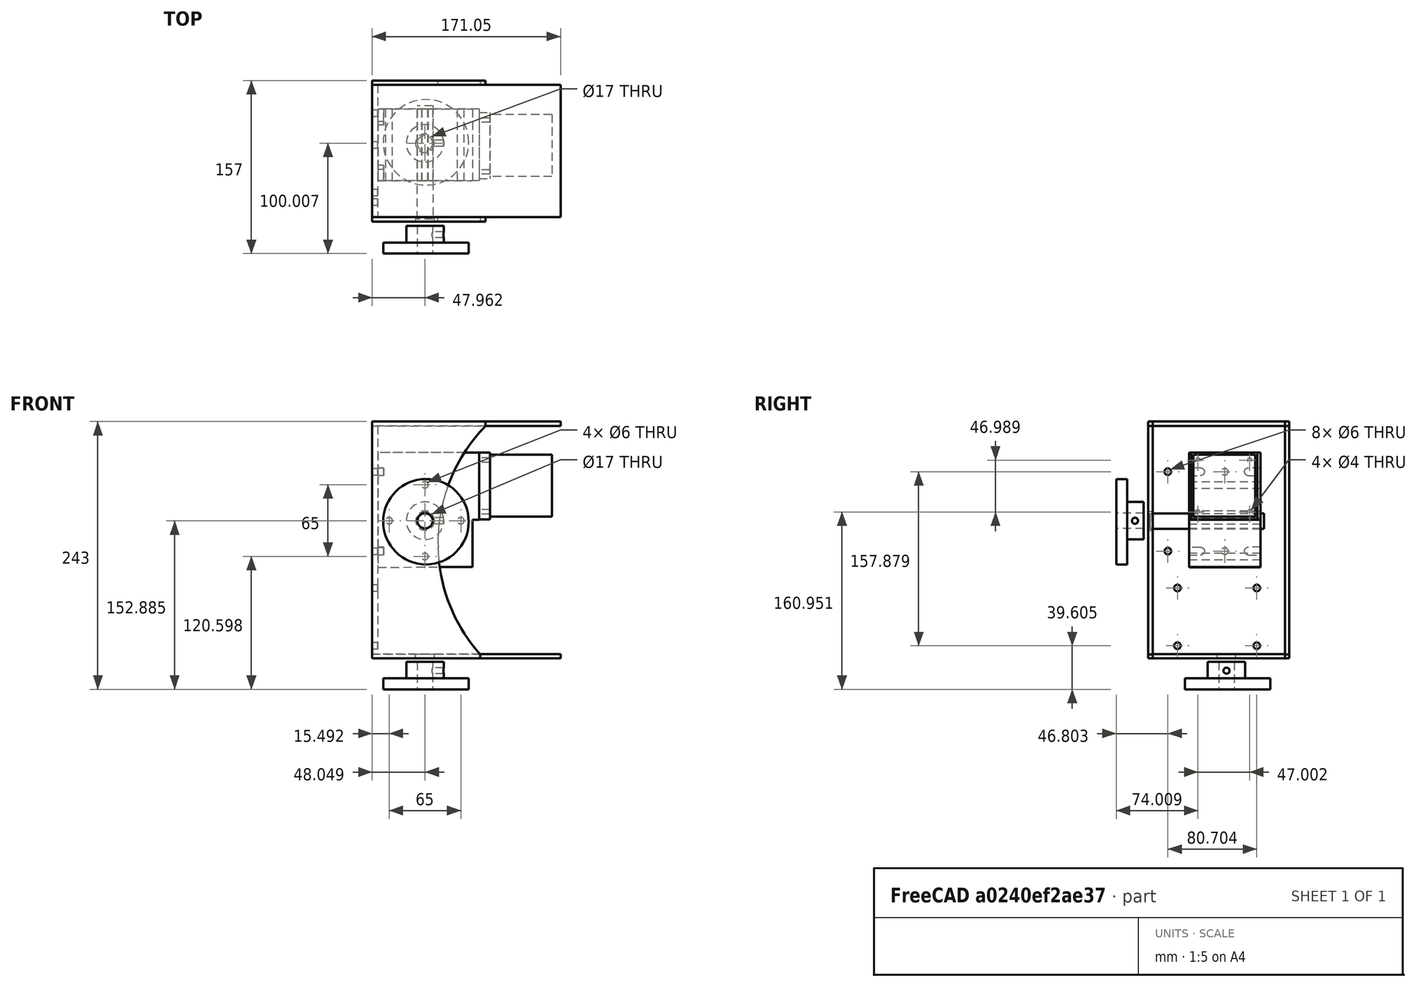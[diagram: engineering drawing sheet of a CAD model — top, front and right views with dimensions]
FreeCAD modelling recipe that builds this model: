
FCSTD DOCUMENT  (FreeCAD 0.19R)
Label: az-el-rotor
License: All rights reserved
LicenseURL: http://en.wikipedia.org/wiki/All_rights_reserved
objects: TechDraw::DrawViewDimension×58, Sketcher::SketchObject×25, PartDesign::Pad×13, TechDraw::DrawViewPart×12, PartDesign::Body×11, PartDesign::Hole×9, App::Link×8, PartDesign::Pocket×3, App::MeasureDistance×3, TechDraw::DrawSVGTemplate×3, TechDraw::DrawPage×3, PartDesign::LinearPattern×2, TechDraw::DrawViewSection×2, App::LinkGroup×2, Image::ImagePlane×1
note: 88 computed .brp shape members not serialized (recipe doc carries the construction recipe); baked Part::Feature solids carry a one-line shape summary decoded from their .brp

FEATURE [Sketcher::SketchObject] Sketch001
  MapMode = 5
  Placement = pos=(0,0,0) rot=(1,0,0;1.5708rad)
  Support = -> [XZ_Plane001]
  sketch-geometry (4):
    g0: LineSegment StartX=-11.8481 StartY=194.05 StartZ=0 EndX=-68.2481 EndY=194.05 EndZ=0
    g1: LineSegment StartX=-68.2481 StartY=194.05 StartZ=0 EndX=-68.2481 EndY=137.65 EndZ=0
    g2: LineSegment StartX=-68.2481 StartY=137.65 StartZ=0 EndX=-11.8481 EndY=137.65 EndZ=0
    g3: LineSegment StartX=-11.8481 StartY=137.65 StartZ=0 EndX=-11.8481 EndY=194.05 EndZ=0
  constraints (10):
    c: Coincident(g0,g1)
    c: Coincident(g1,g2)
    c: Coincident(g2,g3)
    c: Coincident(g3,g0)
    c: Horizontal(g0)
    c: Horizontal(g2)
    c: Vertical(g1)
    c: Vertical(g3)
    c: DistanceX(g0,g0) = 56.4
    c: DistanceY(g3,g3) = 56.4
FEATURE [PartDesign::Pad] Pad
  AllowMultiFace = false
  Direction = (1,1,1)
  Length = 56
  Length2 = 100
  Placement = pos=(0,0,0) rot=(1,0,0;1.5708rad)
  Profile = -> Sketch001
  Type = 0
FEATURE [PartDesign::Body] Body001  label="motor"
  Group = -> [Sketch001,Pad]
  Origin = -> Origin001
  Placement = pos=(81,61,-276) rot=(0,0,1;0rad)
  Tip = -> Pad
FEATURE [Sketcher::SketchObject] Sketch
  MapMode = 5
  Placement = pos=(0,0,0) rot=(1,0,0;1.5708rad)
  Support = -> [XZ_Plane]
  sketch-geometry (4):
    g0: LineSegment StartX=103.932 StartY=89.9717 StartZ=0 EndX=43.9326 EndY=89.9717 EndZ=0
    g1: LineSegment StartX=43.9326 StartY=89.9717 StartZ=0 EndX=43.9326 EndY=29.0926 EndZ=0
    g2: LineSegment StartX=43.9326 StartY=29.0926 StartZ=0 EndX=103.932 EndY=29.0926 EndZ=0
    g3: LineSegment StartX=103.932 StartY=29.0926 StartZ=0 EndX=103.932 EndY=89.9717 EndZ=0
  constraints (8):
    c: Coincident(g0,g1)
    c: Coincident(g1,g2)
    c: Coincident(g2,g3)
    c: Coincident(g3,g0)
    c: Horizontal(g0)
    c: Horizontal(g2)
    c: Vertical(g1)
    c: Vertical(g3)
FEATURE [PartDesign::Pad] Pad001
  AllowMultiFace = false
  Direction = (1,1,1)
  Length = 10
  Length2 = 100
  Placement = pos=(0,0,0) rot=(1,0,0;1.5708rad)
  Profile = -> Sketch
  Type = 0
FEATURE [Sketcher::SketchObject] Sketch002
  MapMode = 5
  Placement = pos=(0,-10,2.2e-15) rot=(1,0,0;1.5708rad)
  Support = -> [Pad001]
  sketch-geometry (8):
    g0: LineSegment [constr] StartX=97.011 StartY=82.9397 StartZ=0 EndX=50.0093 EndY=82.9397 EndZ=0
    g1: LineSegment [constr] StartX=50.0093 StartY=82.9397 StartZ=0 EndX=50.0093 EndY=35.9508 EndZ=0
    g2: LineSegment [constr] StartX=50.0093 StartY=35.9508 StartZ=0 EndX=97.011 EndY=35.9508 EndZ=0
    g3: LineSegment [constr] StartX=97.011 StartY=35.9508 StartZ=0 EndX=97.011 EndY=82.9397 EndZ=0
    g4: Circle CenterX=97.011 CenterY=82.9397 CenterZ=0 NormalX=0 NormalY=0 NormalZ=1 AngleXU=0 Radius=2.60112
    g5: Circle CenterX=50.0093 CenterY=82.9397 CenterZ=0 NormalX=0 NormalY=0 NormalZ=1 AngleXU=0 Radius=2.14953
    g6: Circle CenterX=50.0093 CenterY=35.9508 CenterZ=0 NormalX=0 NormalY=0 NormalZ=1 AngleXU=0 Radius=2.21763
    g7: Circle CenterX=97.011 CenterY=35.9508 CenterZ=0 NormalX=0 NormalY=0 NormalZ=1 AngleXU=0 Radius=2.02514
  constraints (12):
    c: Coincident(g0,g1)
    c: Coincident(g1,g2)
    c: Coincident(g2,g3)
    c: Coincident(g3,g0)
    c: Horizontal(g0)
    c: Horizontal(g2)
    c: Vertical(g1)
    c: Vertical(g3)
    c: Coincident(g4,g0)
    c: Coincident(g5,g0)
    c: Coincident(g6,g1)
    c: Coincident(g7,g2)
FEATURE [PartDesign::Hole] Hole
  AllowMultiFace = false
  BaseFeature = -> Pad001
  Depth = 25
  DepthType = 0
  Diameter = 4
  DrillPoint = 1
  DrillPointAngle = 118
  HoleCutCountersinkAngle = 90
  HoleCutDepth = 0
  HoleCutDiameter = 0
  HoleCutType = 0
  ModelActualThread = false
  Placement = pos=(0,0,0) rot=(1,0,0;1.5708rad)
  Profile = -> Sketch002
  Tapered = false
  TaperedAngle = 90
  ThreadAngle = 0
  ThreadClass = 0
  ThreadCutOffInner = 0
  ThreadCutOffOuter = 0
  ThreadDirection = 0
  ThreadFit = 0
  ThreadPitch = 0
  ThreadSize = 0
  ThreadType = 0
  Threaded = false
FEATURE [PartDesign::Body] Body  label="motor-mount"
  Group = -> [Sketch,Pad001,Sketch002,Hole]
  Origin = -> Origin
  Placement = pos=(3,-41,-170) rot=(0,0,1;1.5708rad)
  Tip = -> Hole
FEATURE [Sketcher::SketchObject] Sketch003
  MapMode = 5
  Placement = pos=(0,0,0) rot=(1,0,0;1.5708rad)
  Support = -> [XZ_Plane002]
  sketch-geometry (9):
    g0: LineSegment [constr] StartX=-113.706 StartY=-142.169 StartZ=0 EndX=6.22488 EndY=-142.169 EndZ=0
    g1: LineSegment [constr] StartX=-45.8819 StartY=-179.611 StartZ=0 EndX=-45.8819 EndY=-105.711 EndZ=0
    g2: Circle [constr] CenterX=-45.9137 CenterY=-142.169 CenterZ=0 NormalX=0 NormalY=0 NormalZ=1 AngleXU=0 Radius=32.5
    g3: LineSegment StartX=3 StartY=-80 StartZ=0 EndX=-88.6238 EndY=-80 EndZ=0
    g4: LineSegment StartX=-88.6238 StartY=-80 StartZ=0 EndX=-88.5635 EndY=-184.211 EndZ=0
    g5: LineSegment StartX=-88.5635 StartY=-184.211 StartZ=0 EndX=-3 EndY=-184 EndZ=0
    g6: LineSegment StartX=-3 StartY=-184 StartZ=0 EndX=-3 EndY=-141 EndZ=0
    g7: LineSegment StartX=3 StartY=-141 StartZ=0 EndX=-3 EndY=-141 EndZ=0
    g8: LineSegment StartX=3 StartY=-141 StartZ=0 EndX=3 EndY=-80 EndZ=0
  constraints (6):
    c: Horizontal(g0)
    c: Vertical(g1)
    c: PointOnObject(g2,g0)
    c: Diameter(g2) = 65
    c: Coincident(g3,g4)
    c: Coincident(g4,g5)
FEATURE [PartDesign::Pad] Pad002
  AllowMultiFace = false
  Direction = (1,1,1)
  Length = 65
  Length2 = 100
  Placement = pos=(0,0,0) rot=(1,0,0;1.5708rad)
  Profile = -> Sketch003
  Type = 0
FEATURE [Sketcher::SketchObject] Sketch004
  MapMode = 5
  Placement = pos=(0,-65,1.43e-14) rot=(1,0,0;1.5708rad)
  Support = -> [Pad002]
  sketch-geometry (6):
    g0: Circle [constr] CenterX=-46.0078 CenterY=-141.902 CenterZ=0 NormalX=0 NormalY=0 NormalZ=1 AngleXU=0 Radius=32.5
    g1: LineSegment [constr] StartX=-46.0078 StartY=-141.902 StartZ=0 EndX=-46.0078 EndY=-102 EndZ=0
    g2: Circle CenterX=-46 CenterY=-109.402 CenterZ=0 NormalX=0 NormalY=0 NormalZ=1 AngleXU=0 Radius=3.60206
    g3: Circle CenterX=-13.5079 CenterY=-142 CenterZ=0 NormalX=0 NormalY=0 NormalZ=1 AngleXU=0 Radius=2.2381
    g4: Circle CenterX=-46 CenterY=-174.402 CenterZ=0 NormalX=0 NormalY=0 NormalZ=1 AngleXU=0 Radius=2.56856
    g5: Circle CenterX=-78.5076 CenterY=-142 CenterZ=0 NormalX=0 NormalY=0 NormalZ=1 AngleXU=0 Radius=1.48182
  constraints (7):
    c: Diameter(g0) = 65
    c: Coincident(g1,g0)
    c: Vertical(g1)
    c: PointOnObject(g2,g0)
    c: PointOnObject(g3,g0)
    c: PointOnObject(g4,g0)
    c: PointOnObject(g5,g0)
FEATURE [PartDesign::Hole] Hole001
  AllowMultiFace = false
  BaseFeature = -> Pad002
  Depth = 72
  DepthType = 0
  Diameter = 6
  DrillPoint = 1
  DrillPointAngle = 118
  HoleCutCountersinkAngle = 90
  HoleCutDepth = 0
  HoleCutDiameter = 0
  HoleCutType = 0
  ModelActualThread = false
  Placement = pos=(0,0,0) rot=(1,0,0;1.5708rad)
  Profile = -> Sketch004
  Tapered = false
  TaperedAngle = 90
  ThreadAngle = 0
  ThreadClass = 0
  ThreadCutOffInner = 0
  ThreadCutOffOuter = 0
  ThreadDirection = 0
  ThreadFit = 0
  ThreadPitch = 0
  ThreadSize = 0
  ThreadType = 0
  Threaded = false
FEATURE [Sketcher::SketchObject] Sketch005
  MapMode = 5
  Placement = pos=(0,-65,1.43e-14) rot=(1,0,0;1.5708rad)
  Support = -> [Hole001]
  sketch-geometry (5):
    g0: ArcOfCircle CenterX=-45.9597 CenterY=-141.985 CenterZ=0 NormalX=0 NormalY=0 NormalZ=1 AngleXU=0 Radius=7 StartAngle=1.94945 EndAngle=7.48847
    g1: LineSegment [constr] StartX=-48.5474 StartY=-132.991 StartZ=0 EndX=-43.4577 EndY=-132.991 EndZ=0
    g2: LineSegment StartX=-48.5474 StartY=-135.481 StartZ=0 EndX=-48.5474 EndY=-132.991 EndZ=0
    g3: LineSegment StartX=-48.5474 StartY=-132.991 StartZ=0 EndX=-43.4577 EndY=-132.991 EndZ=0
    g4: LineSegment StartX=-43.4577 StartY=-132.991 StartZ=0 EndX=-43.4577 EndY=-135.447 EndZ=0
  constraints (8):
    c: Horizontal(g1)
    c: Coincident(g2,g1)
    c: Vertical(g2)
    c: Coincident(g3,g1)
    c: Vertical(g4)
    c: Coincident(g2,g3)
    c: Coincident(g0,g4)
    c: Coincident(g3,g4)
FEATURE [PartDesign::Pocket] Pocket
  AllowMultiFace = false
  BaseFeature = -> Hole001
  Length = 72
  Length2 = 100
  Placement = pos=(0,0,0) rot=(1,0,0;1.5708rad)
  Profile = -> Sketch005
  Type = 0
FEATURE [Sketcher::SketchObject] Sketch006
  MapMode = 5
  Placement = pos=(0,0,0) rot=(1,0,0;1.5708rad)
  Support = -> [XZ_Plane003]
  sketch-geometry (1):
    g0: Circle CenterX=-37.9108 CenterY=-368.292 CenterZ=0 NormalX=0 NormalY=0 NormalZ=1 AngleXU=0 Radius=7
  constraints (1):
    c: Diameter(g0) = 14
FEATURE [PartDesign::Pad] Pad003
  AllowMultiFace = false
  Direction = (1,1,1)
  Length = 103
  Length2 = 100
  Placement = pos=(0,0,0) rot=(1,0,0;1.5708rad)
  Profile = -> Sketch006
  Type = 0
FEATURE [PartDesign::Body] Body003
  Group = -> [Sketch006,Pad003]
  Origin = -> Origin003
  Placement = pos=(-8,69,226) rot=(0,0,1;0rad)
  Tip = -> Pad003
FEATURE [Image::ImagePlane] ImagePlane
  Placement = pos=(-89,114,-7) rot=(-0.57735,0.57735,0.57735;4.18879rad)
  XSize = 257.083
  YSize = 755.483
FEATURE [Sketcher::SketchObject] Sketch007
  MapMode = 5
  Placement = pos=(-88.6701,0,-0.0513552) rot=(0.707312,0,-0.706902;3.14159rad)
  Support = -> [Pocket]
  sketch-geometry (4):
    g0: LineSegment StartX=94 StartY=65.9617 StartZ=0 EndX=101.06 EndY=65.9617 EndZ=0
    g1: LineSegment StartX=101.06 StartY=65.9617 StartZ=0 EndX=101.06 EndY=54.6023 EndZ=0
    g2: LineSegment StartX=94 StartY=54.5531 StartZ=0 EndX=94 EndY=65.9617 EndZ=0
    g3: ArcOfCircle CenterX=97.5304 CenterY=54.5531 CenterZ=0 NormalX=0 NormalY=0 NormalZ=1 AngleXU=0 Radius=3.53039 StartAngle=3.14159 EndAngle=6.29711
  constraints (7):
    c: Coincident(g0,g1)
    c: Coincident(g2,g0)
    c: Horizontal(g0)
    c: Vertical(g1)
    c: Vertical(g2)
    c: Coincident(g3,g1)
    c: Coincident(g2,g3)
FEATURE [PartDesign::Pocket] Pocket001
  AllowMultiFace = false
  BaseFeature = -> Pocket
  Length = 5
  Length2 = 100
  Placement = pos=(0,0,0) rot=(1,0,0;1.5708rad)
  Profile = -> Sketch007
  Type = 0
FEATURE [PartDesign::LinearPattern] LinearPattern
  BaseFeature = -> Pocket001
  Direction = -> Sketch007 [H_Axis]
  Length = 72
  Occurrences = 2
  Originals = -> [Pocket001]
  Placement = pos=(0,0,0) rot=(1,0,0;1.5708rad)
FEATURE [Sketcher::SketchObject] Sketch008
  MapMode = 5
  Placement = pos=(-88.6701,0,-0.0513552) rot=(0.707312,0,-0.706902;3.14159rad)
  Support = -> [LinearPattern]
  sketch-geometry (5):
    g0: LineSegment [constr] StartX=97.5242 StartY=54.9703 StartZ=0 EndX=97.5242 EndY=-5.59938 EndZ=0
    g1: ArcOfCircle CenterX=97.5242 CenterY=11.0213 CenterZ=0 NormalX=0 NormalY=0 NormalZ=1 AngleXU=0 Radius=3.60435 StartAngle=6.27818 EndAngle=9.4465
    g2: LineSegment StartX=101.128 StartY=11.0032 StartZ=0 EndX=101.128 EndY=-1.64086 EndZ=0
    g3: LineSegment StartX=101.128 StartY=-1.64086 StartZ=0 EndX=93.9207 EndY=-1.64086 EndZ=0
    g4: LineSegment StartX=93.9207 StartY=-1.64086 StartZ=0 EndX=93.9207 EndY=10.943 EndZ=0
  constraints (9):
    c: Vertical(g0)
    c: PointOnObject(g1,g0)
    c: Coincident(g2,g3)
    c: Coincident(g3,g4)
    c: Horizontal(g3)
    c: Vertical(g2)
    c: Vertical(g4)
    c: Coincident(g1,g4)
    c: Coincident(g2,g1)
FEATURE [PartDesign::Pocket] Pocket002
  AllowMultiFace = false
  BaseFeature = -> LinearPattern
  Length = 5
  Length2 = 100
  Placement = pos=(0,0,0) rot=(1,0,0;1.5708rad)
  Profile = -> Sketch008
  Type = 0
FEATURE [PartDesign::LinearPattern] LinearPattern001
  BaseFeature = -> Pocket002
  Direction = -> Sketch008 [H_Axis]
  Length = 72
  Occurrences = 2
  Originals = -> [Pocket002]
  Placement = pos=(0,0,0) rot=(1,0,0;1.5708rad)
FEATURE [PartDesign::Body] Body002  label="gearbox"
  Group = -> [Sketch003,Pad002,Sketch004,Hole001,Sketch005,Pocket,Sketch007,Pocket001,LinearPattern,Sketch008,Pocket002,LinearPattern001]
  Origin = -> Origin002
  Placement = pos=(0,66,0) rot=(0,0,1;0rad)
  Tip = -> LinearPattern001
FEATURE [Sketcher::SketchObject] Sketch011
  MapMode = 5
  Support = -> [XY_Plane005]
  sketch-geometry (4):
    g0: LineSegment StartX=-94 StartY=88 StartZ=0 EndX=77.053 EndY=88 EndZ=0
    g1: LineSegment StartX=77.053 StartY=88 StartZ=0 EndX=77.053 EndY=-32 EndZ=0
    g2: LineSegment StartX=77.053 StartY=-32 StartZ=0 EndX=-94 EndY=-32 EndZ=0
    g3: LineSegment StartX=-94 StartY=-32 StartZ=0 EndX=-94 EndY=88 EndZ=0
  constraints (8):
    c: Coincident(g0,g1)
    c: Coincident(g1,g2)
    c: Coincident(g2,g3)
    c: Coincident(g3,g0)
    c: Horizontal(g0)
    c: Horizontal(g2)
    c: Vertical(g1)
    c: Vertical(g3)
FEATURE [PartDesign::Pad] Pad005
  AllowMultiFace = false
  Direction = (1,1,1)
  Length = 4
  Length2 = 100
  Profile = -> Sketch011
  Type = 0
FEATURE [PartDesign::Body] Body005  label="top-plate"
  Group = -> [Sketch011,Pad005]
  Origin = -> Origin005
  Placement = pos=(0,0,-56) rot=(0,0,1;0rad)
  Tip = -> Pad005
FEATURE [Sketcher::SketchObject] Sketch012
  MapMode = 5
  Support = -> [XY_Plane006]
  sketch-geometry (4):
    g0: LineSegment StartX=-93.9912 StartY=88.0053 StartZ=0 EndX=77 EndY=88.0053 EndZ=0
    g1: LineSegment StartX=77 StartY=88.0053 StartZ=0 EndX=77 EndY=-32 EndZ=0
    g2: LineSegment StartX=77 StartY=-32 StartZ=0 EndX=-93.9912 EndY=-32 EndZ=0
    g3: LineSegment StartX=-93.9912 StartY=-32 StartZ=0 EndX=-93.9912 EndY=88.0053 EndZ=0
  constraints (8):
    c: Coincident(g0,g1)
    c: Coincident(g1,g2)
    c: Coincident(g2,g3)
    c: Coincident(g3,g0)
    c: Horizontal(g0)
    c: Horizontal(g2)
    c: Vertical(g1)
    c: Vertical(g3)
FEATURE [PartDesign::Pad] Pad006
  AllowMultiFace = false
  Direction = (1,1,1)
  Length = 4
  Length2 = 100
  Profile = -> Sketch012
  Type = 0
FEATURE [Sketcher::SketchObject] Sketch013
  MapMode = 5
  Placement = pos=(0,0,0) rot=(1,0,0;3.14159rad)
  Support = -> [Pad006]
  sketch-geometry (1):
    g0: Circle CenterX=-46.0384 CenterY=-35.0069 CenterZ=0 NormalX=0 NormalY=0 NormalZ=1 AngleXU=0 Radius=10.0299
FEATURE [PartDesign::Hole] Hole003
  AllowMultiFace = false
  BaseFeature = -> Pad006
  Depth = 10
  DepthType = 0
  Diameter = 17
  DrillPoint = 1
  DrillPointAngle = 118
  HoleCutCountersinkAngle = 90
  HoleCutDepth = 0
  HoleCutDiameter = 0
  HoleCutType = 0
  ModelActualThread = false
  Profile = -> Sketch013
  Tapered = false
  TaperedAngle = 90
  ThreadAngle = 0
  ThreadClass = 0
  ThreadCutOffInner = 0
  ThreadCutOffOuter = 0
  ThreadDirection = 0
  ThreadFit = 0
  ThreadPitch = 0
  ThreadSize = 0
  ThreadType = 0
  Threaded = false
FEATURE [PartDesign::Body] Body006  label="bottom-plate"
  Group = -> [Sketch012,Pad006,Sketch013,Hole003]
  Origin = -> Origin006
  Placement = pos=(0,0,-267) rot=(0,0,1;0rad)
  Tip = -> Hole003
FEATURE [Sketcher::SketchObject] Sketch014
  MapMode = 5
  Support = -> [XY_Plane007]
  sketch-geometry (1):
    g0: Circle CenterX=-46.1126 CenterY=35.0755 CenterZ=0 NormalX=0 NormalY=0 NormalZ=1 AngleXU=0 Radius=38.7738
FEATURE [PartDesign::Pad] Pad007
  AllowMultiFace = false
  Direction = (1,1,1)
  Length = 10
  Length2 = 100
  Profile = -> Sketch014
  Type = 0
FEATURE [Sketcher::SketchObject] Sketch015
  MapMode = 5
  Placement = pos=(0,0,0) rot=(1,0,0;3.14159rad)
  Support = -> [Pad007]
  sketch-geometry (4):
    g0: LineSegment [constr] StartX=-47 StartY=5 StartZ=0 EndX=-47 EndY=-81 EndZ=0
    g1: LineSegment [constr] StartX=-86 StartY=-36 StartZ=0 EndX=-6 EndY=-36 EndZ=0
    g2: Circle [constr] CenterX=-47 CenterY=-36 CenterZ=0 NormalX=0 NormalY=0 NormalZ=1 AngleXU=0 Radius=7
    g3: Circle CenterX=-47 CenterY=-36 CenterZ=0 NormalX=0 NormalY=0 NormalZ=1 AngleXU=0 Radius=17
  constraints (5):
    c: Vertical(g0)
    c: Horizontal(g1)
    c: PointOnObject(g2,g0)
    c: Diameter(g2) = 14
    c: Coincident(g3,g2)
FEATURE [PartDesign::Pad] Pad008
  AllowMultiFace = false
  BaseFeature = -> Pad007
  Direction = (1,1,1)
  Length = 15
  Length2 = 100
  Profile = -> Sketch015
  Type = 0
FEATURE [Sketcher::SketchObject] Sketch016
  MapMode = 5
  Placement = pos=(0,0,-15) rot=(1,0,0;3.14159rad)
  Support = -> [Pad008]
  sketch-geometry (3):
    g0: LineSegment [constr] StartX=-47.0041 StartY=-17.9869 StartZ=0 EndX=-47.0041 EndY=-57.2105 EndZ=0
    g1: LineSegment [constr] StartX=-67.0883 StartY=-35.9976 StartZ=0 EndX=-26.7183 EndY=-35.9976 EndZ=0
    g2: Circle CenterX=-47.0247 CenterY=-35.9976 CenterZ=0 NormalX=0 NormalY=0 NormalZ=1 AngleXU=0 Radius=7
  constraints (4):
    c: Vertical(g0)
    c: Horizontal(g1)
    c: PointOnObject(g2,g1)
    c: Diameter(g2) = 14
FEATURE [PartDesign::Hole] Hole004
  AllowMultiFace = false
  BaseFeature = -> Pad008
  Depth = 33
  DepthType = 0
  Diameter = 14
  DrillPoint = 1
  DrillPointAngle = 118
  HoleCutCountersinkAngle = 90
  HoleCutDepth = 0
  HoleCutDiameter = 0
  HoleCutType = 0
  ModelActualThread = false
  Profile = -> Sketch016
  Tapered = false
  TaperedAngle = 90
  ThreadAngle = 0
  ThreadClass = 0
  ThreadCutOffInner = 0
  ThreadCutOffOuter = 0
  ThreadDirection = 0
  ThreadFit = 0
  ThreadPitch = 0
  ThreadSize = 0
  ThreadType = 0
  Threaded = false
FEATURE [Sketcher::SketchObject] Sketch017
  MapMode = 5
  Placement = pos=(0,0,0) rot=(0.57735,0.57735,0.57735;2.0944rad)
  Support = -> [YZ_Plane007]
  sketch-geometry (1):
    g0: Circle CenterX=35.9745 CenterY=-6.96869 CenterZ=0 NormalX=0 NormalY=0 NormalZ=1 AngleXU=0 Radius=2.5
  constraints (1):
    c: Diameter(g0) = 5
FEATURE [PartDesign::Hole] Hole005
  AllowMultiFace = false
  BaseFeature = -> Hole004
  Depth = 43
  DepthType = 0
  Diameter = 5.5
  DrillPoint = 1
  DrillPointAngle = 118
  HoleCutCountersinkAngle = 90
  HoleCutDepth = 0
  HoleCutDiameter = 5
  HoleCutType = 0
  ModelActualThread = false
  Profile = -> Sketch017
  Tapered = false
  TaperedAngle = 90
  ThreadAngle = 60
  ThreadClass = 0
  ThreadCutOffInner = 0.0866025
  ThreadCutOffOuter = 0.173205
  ThreadDirection = 0
  ThreadFit = 0
  ThreadPitch = 0.8
  ThreadSize = 0
  ThreadType = 0
  Threaded = false
FEATURE [PartDesign::Body] Body007  label="adapter"
  Group = -> [Sketch014,Pad007,Sketch015,Pad008,Sketch016,Hole004,Sketch017,Hole005]
  Origin = -> Origin007
  Placement = pos=(1,71,-285) rot=(1,0,0;3.14159rad)
  Tip = -> Hole005
FEATURE [Sketcher::SketchObject] Sketch018
  MapMode = 5
  Placement = pos=(0,0,0) rot=(1,0,0;1.5708rad)
  Support = -> [XZ_Plane008]
  sketch-geometry (7):
    g0: LineSegment StartX=-94 StartY=-52 StartZ=0 EndX=-94 EndY=-267 EndZ=0
    g1: LineSegment StartX=-94 StartY=-267 StartZ=0 EndX=3.97419 EndY=-267 EndZ=0
    g2: LineSegment StartX=9 StartY=-52 StartZ=0 EndX=-94 EndY=-52 EndZ=0
    g3: Circle [constr] CenterX=9 CenterY=-52 CenterZ=0 NormalX=0 NormalY=0 NormalZ=1 AngleXU=0 Radius=10
    g4: LineSegment StartX=9 StartY=-52 StartZ=0 EndX=9 EndY=-56 EndZ=0
    g5: LineSegment StartX=3.97419 StartY=-267 StartZ=0 EndX=3.97419 EndY=-263.283 EndZ=0
    g6: ArcOfCircle CenterX=117.845 CenterY=-162.341 CenterZ=0 NormalX=0 NormalY=0 NormalZ=1 AngleXU=0 Radius=152.17 StartAngle=2.36783 EndAngle=3.86687
  constraints (12):
    c: Vertical(g0)
    c: Coincident(g0,g1)
    c: Horizontal(g1)
    c: Coincident(g2,g0)
    c: Horizontal(g2)
    c: Coincident(g3,g2)
    c: Coincident(g4,g2)
    c: Vertical(g4)
    c: Vertical(g5)
    c: Coincident(g6,g4)
    c: Coincident(g6,g5)
    c: Coincident(g1,g5)
FEATURE [PartDesign::Pad] Pad009
  AllowMultiFace = false
  Direction = (1,1,1)
  Length = 4
  Length2 = 100
  Placement = pos=(0,0,0) rot=(1,0,0;1.5708rad)
  Profile = -> Sketch018
  Type = 0
FEATURE [Sketcher::SketchObject] Sketch019
  MapMode = 5
  Placement = pos=(0,0,0) rot=(1,0,0;1.5708rad)
  Support = -> [XZ_Plane009]
  sketch-geometry (7):
    g0: LineSegment StartX=-94 StartY=-52 StartZ=0 EndX=-94 EndY=-267 EndZ=0
    g1: LineSegment StartX=-94 StartY=-267 StartZ=0 EndX=3.97419 EndY=-267 EndZ=0
    g2: LineSegment StartX=9 StartY=-52 StartZ=0 EndX=-94 EndY=-52 EndZ=0
    g3: Circle [constr] CenterX=9 CenterY=-52 CenterZ=0 NormalX=0 NormalY=0 NormalZ=1 AngleXU=0 Radius=10
    g4: LineSegment StartX=9 StartY=-52 StartZ=0 EndX=9 EndY=-56 EndZ=0
    g5: LineSegment StartX=3.97419 StartY=-267 StartZ=0 EndX=3.97419 EndY=-263.283 EndZ=0
    g6: ArcOfCircle CenterX=117.845 CenterY=-162.341 CenterZ=0 NormalX=0 NormalY=0 NormalZ=1 AngleXU=0 Radius=152.17 StartAngle=2.36783 EndAngle=3.86687
  constraints (12):
    c: Vertical(g0)
    c: Coincident(g0,g1)
    c: Horizontal(g1)
    c: Coincident(g2,g0)
    c: Horizontal(g2)
    c: Coincident(g3,g2)
    c: Coincident(g4,g2)
    c: Vertical(g4)
    c: Vertical(g5)
    c: Coincident(g6,g4)
    c: Coincident(g6,g5)
    c: Coincident(g1,g5)
FEATURE [PartDesign::Pad] Pad010
  AllowMultiFace = false
  Direction = (1,1,1)
  Length = 4
  Length2 = 100
  Placement = pos=(0,0,0) rot=(1,0,0;1.5708rad)
  Profile = -> Sketch019
  Type = 0
FEATURE [PartDesign::Body] Body009  label="sideplate002"
  Group = -> [Sketch019,Pad010]
  Origin = -> Origin009
  Placement = pos=(0,92,0) rot=(0,0,1;0rad)
  Tip = -> Pad010
FEATURE [Sketcher::SketchObject] Sketch020
  MapMode = 5
  Placement = pos=(0,-4,9e-16) rot=(1,0,0;1.5708rad)
  Support = -> [Pad009]
  sketch-geometry (1):
    g0: Circle CenterX=-45.9514 CenterY=-142.115 CenterZ=0 NormalX=0 NormalY=0 NormalZ=1 AngleXU=0 Radius=8.75
  constraints (1):
    c: Diameter(g0) = 17.5
FEATURE [PartDesign::Hole] Hole006
  AllowMultiFace = false
  BaseFeature = -> Pad009
  Depth = 25
  DepthType = 0
  Diameter = 17
  DrillPoint = 1
  DrillPointAngle = 118
  HoleCutCountersinkAngle = 90
  HoleCutDepth = 0
  HoleCutDiameter = 0
  HoleCutType = 0
  ModelActualThread = false
  Placement = pos=(0,0,0) rot=(1,0,0;1.5708rad)
  Profile = -> Sketch020
  Tapered = false
  TaperedAngle = 90
  ThreadAngle = 0
  ThreadClass = 0
  ThreadCutOffInner = 0
  ThreadCutOffOuter = 0
  ThreadDirection = 0
  ThreadFit = 0
  ThreadPitch = 0
  ThreadSize = 0
  ThreadType = 0
  Threaded = false
FEATURE [PartDesign::Body] Body008  label="sideplate1"
  Group = -> [Sketch018,Pad009,Sketch020,Hole006]
  Origin = -> Origin008
  Placement = pos=(0,-32,0) rot=(0,0,1;0rad)
  Tip = -> Hole006
FEATURE [App::MeasureDistance] Distance  label="Distance: 128,00 mm"
  Distance = 128
  P1 = (9,-36,-52)
  P2 = (9,92,-52)
FEATURE [App::MeasureDistance] Distance001  label="Distance: 171,01 mm"
  Distance = 171.008
  P1 = (-93.908,-36,-52)
  P2 = (77.053,-32,-52)
FEATURE [App::MeasureDistance] Distance002  label="Distance: 214,93 mm"
  Distance = 214.93
  P1 = (-94,-36,-52.0699)
  P2 = (-93.9454,-36,-267)
FEATURE [TechDraw::DrawSVGTemplate] Template
  Height = 594
  Orientation = 1
  Width = 841
FEATURE [TechDraw::DrawPage] Page
  KeepUpdated = true
  NextBalloonIndex = 1
  ProjectionType = 0
  Template = -> Template
FEATURE [Sketcher::SketchObject] Sketch009
  MapMode = 5
  Placement = pos=(0,0,0) rot=(0.57735,0.57735,0.57735;2.0944rad)
  Support = -> [YZ_Plane004]
  sketch-geometry (24):
    g0: LineSegment [constr] StartX=-28 StartY=-262 StartZ=0 EndX=78 EndY=-262 EndZ=0
    g1: LineSegment [constr] StartX=78 StartY=-262 StartZ=0 EndX=78 EndY=-263 EndZ=0
    g2: LineSegment [constr] StartX=78 StartY=-263 StartZ=0 EndX=-28 EndY=-263 EndZ=0
    g3: LineSegment [constr] StartX=-28 StartY=-263 StartZ=0 EndX=-28 EndY=-262 EndZ=0
    g4: LineSegment [constr] StartX=78 StartY=-263 StartZ=0 EndX=88 EndY=-263 EndZ=0
    g5: LineSegment [constr] StartX=88 StartY=-263 StartZ=0 EndX=88 EndY=-80 EndZ=0
    g6: LineSegment [constr] StartX=88 StartY=-80 StartZ=0 EndX=78 EndY=-80 EndZ=0
    g7: LineSegment [constr] StartX=78 StartY=-80 StartZ=0 EndX=78 EndY=-263 EndZ=0
    g8: LineSegment [constr] StartX=88 StartY=-80 StartZ=0 EndX=78 EndY=-80 EndZ=0
    g9: LineSegment [constr] StartX=78 StartY=-80 StartZ=0 EndX=78 EndY=-60 EndZ=0
    g10: LineSegment [constr] StartX=78 StartY=-60 StartZ=0 EndX=88 EndY=-60 EndZ=0
    g11: LineSegment [constr] StartX=88 StartY=-60 StartZ=0 EndX=88 EndY=-80 EndZ=0
    g12: LineSegment [constr] StartX=88 StartY=-60 StartZ=0 EndX=-41 EndY=-60 EndZ=0
    g13: LineSegment [constr] StartX=-41 StartY=-60 StartZ=0 EndX=-41 EndY=-56 EndZ=0
    g14: LineSegment [constr] StartX=-41 StartY=-56 StartZ=0 EndX=88 EndY=-56 EndZ=0
    g15: LineSegment [constr] StartX=88 StartY=-56 StartZ=0 EndX=88 EndY=-60 EndZ=0
    g16: LineSegment [constr] StartX=-28 StartY=-263 StartZ=0 EndX=-32 EndY=-263 EndZ=0
    g17: LineSegment [constr] StartX=-32 StartY=-263 StartZ=0 EndX=-32 EndY=-53 EndZ=0
    g18: LineSegment [constr] StartX=-32 StartY=-53 StartZ=0 EndX=-28 EndY=-53 EndZ=0
    g19: LineSegment [constr] StartX=-28 StartY=-53 StartZ=0 EndX=-28 EndY=-263 EndZ=0
    g20: LineSegment StartX=88 StartY=-263 StartZ=0 EndX=-32 EndY=-263 EndZ=0
    g21: LineSegment StartX=-32 StartY=-263 StartZ=0 EndX=-32 EndY=-56 EndZ=0
    g22: LineSegment StartX=-32 StartY=-56 StartZ=0 EndX=88 EndY=-56 EndZ=0
    g23: LineSegment StartX=88 StartY=-56 StartZ=0 EndX=88 EndY=-263 EndZ=0
  constraints (53):
    c: Coincident(g0,g1)
    c: Coincident(g1,g2)
    c: Coincident(g2,g3)
    c: Coincident(g3,g0)
    c: Horizontal(g0)
    c: Horizontal(g2)
    c: Vertical(g1)
    c: Vertical(g3)
    c: Coincident(g4,g5)
    c: Coincident(g5,g6)
    c: Coincident(g6,g7)
    c: Coincident(g7,g4)
    c: Horizontal(g4)
    c: Horizontal(g6)
    c: Vertical(g5)
    c: Vertical(g7)
    c: Coincident(g4,g1)
    c: Coincident(g8,g9)
    c: Coincident(g9,g10)
    c: Coincident(g10,g11)
    c: Coincident(g11,g8)
    c: Horizontal(g8)
    c: Horizontal(g10)
    c: Vertical(g9)
    c: Vertical(g11)
    c: Coincident(g12,g13)
    c: Coincident(g13,g14)
    c: Coincident(g14,g15)
    c: Coincident(g15,g12)
    c: Horizontal(g12)
    c: Horizontal(g14)
    c: Vertical(g13)
    c: Vertical(g15)
    c: Coincident(g12,g10)
    c: Coincident(g16,g17)
    c: Coincident(g17,g18)
    c: Coincident(g18,g19)
    c: Coincident(g19,g16)
    c: Horizontal(g16)
    c: Horizontal(g18)
    c: Vertical(g17)
    c: Vertical(g19)
    c: Coincident(g16,g2)
    c: Coincident(g20,g21)
    c: Coincident(g21,g22)
    c: Coincident(g22,g23)
    c: Coincident(g23,g20)
    c: Horizontal(g20)
    c: Horizontal(g22)
    c: Vertical(g21)
    c: Vertical(g23)
    c: Coincident(g20,g4)
    c: PointOnObject(g21,g17)
FEATURE [PartDesign::Pad] Pad004
  AllowMultiFace = false
  Direction = (1,1,1)
  Length = 5
  Length2 = 100
  Placement = pos=(0,0,0) rot=(0.57735,0.57735,0.57735;2.0944rad)
  Profile = -> Sketch009
  Type = 0
FEATURE [Sketcher::SketchObject] Sketch010
  MapMode = 5
  Placement = pos=(4e-16,0,0) rot=(0.57735,0.57735,-0.57735;4.18879rad)
  Support = -> [Pad004]
  sketch-geometry (16):
    g0: Circle CenterX=33.537 CenterY=97.5713 CenterZ=0 NormalX=0 NormalY=0 NormalZ=1 AngleXU=0 Radius=3.67394
    g1: Circle CenterX=-18.1974 CenterY=97.5163 CenterZ=0 NormalX=0 NormalY=0 NormalZ=1 AngleXU=0 Radius=3.49495
    g2: LineSegment [constr] StartX=33.537 StartY=97.5713 StartZ=0 EndX=-18.1875 EndY=97.5713 EndZ=0
    g3: LineSegment [constr] StartX=-18.1875 StartY=97.5713 StartZ=0 EndX=-18.1875 EndY=169.553 EndZ=0
    g4: LineSegment [constr] StartX=-18.1875 StartY=169.553 StartZ=0 EndX=33.537 EndY=169.553 EndZ=0
    g5: LineSegment [constr] StartX=33.537 StartY=169.553 StartZ=0 EndX=33.537 EndY=97.5713 EndZ=0
    g6: Circle CenterX=-18.1875 CenterY=169.553 CenterZ=0 NormalX=0 NormalY=0 NormalZ=1 AngleXU=0 Radius=3.5641
    g7: Circle CenterX=33.537 CenterY=169.553 CenterZ=0 NormalX=0 NormalY=0 NormalZ=1 AngleXU=0 Radius=3.59605
    g8: LineSegment [constr] StartX=-9.48692 StartY=255.395 StartZ=0 EndX=62.5067 EndY=255.395 EndZ=0
    g9: LineSegment [constr] StartX=62.5067 StartY=255.395 StartZ=0 EndX=62.5067 EndY=203.001 EndZ=0
    g10: LineSegment [constr] StartX=62.5067 StartY=203.001 StartZ=0 EndX=-9.48692 EndY=203.001 EndZ=0
    g11: LineSegment [constr] StartX=-9.48692 StartY=203.001 StartZ=0 EndX=-9.48692 EndY=255.395 EndZ=0
    g12: Circle CenterX=-9.48692 CenterY=255.395 CenterZ=0 NormalX=0 NormalY=0 NormalZ=1 AngleXU=0 Radius=3.50608
    g13: Circle CenterX=62.5067 CenterY=255.395 CenterZ=0 NormalX=0 NormalY=0 NormalZ=1 AngleXU=0 Radius=3.47701
    g14: Circle CenterX=62.5067 CenterY=203.001 CenterZ=0 NormalX=0 NormalY=0 NormalZ=1 AngleXU=0 Radius=3.61631
    g15: Circle CenterX=-9.48692 CenterY=203.001 CenterZ=0 NormalX=0 NormalY=0 NormalZ=1 AngleXU=0 Radius=3.60277
  constraints (23):
    c: Coincident(g2,g3)
    c: Coincident(g3,g4)
    c: Coincident(g4,g5)
    c: Coincident(g5,g2)
    c: Horizontal(g2)
    c: Horizontal(g4)
    c: Vertical(g3)
    c: Vertical(g5)
    c: Coincident(g2,g0)
    c: Coincident(g6,g3)
    c: Coincident(g7,g4)
    c: Coincident(g8,g9)
    c: Coincident(g9,g10)
    c: Coincident(g10,g11)
    c: Coincident(g11,g8)
    c: Horizontal(g8)
    c: Horizontal(g10)
    c: Vertical(g9)
    c: Vertical(g11)
    c: Coincident(g12,g8)
    c: Coincident(g13,g8)
    c: Coincident(g14,g9)
    c: Coincident(g15,g10)
FEATURE [PartDesign::Hole] Hole002
  AllowMultiFace = false
  BaseFeature = -> Pad004
  Depth = 7
  DepthType = 0
  Diameter = 6
  DrillPoint = 1
  DrillPointAngle = 118
  HoleCutCountersinkAngle = 90
  HoleCutDepth = 0
  HoleCutDiameter = 0
  HoleCutType = 0
  ModelActualThread = false
  Placement = pos=(0,0,0) rot=(0.57735,0.57735,0.57735;2.0944rad)
  Profile = -> Sketch010
  Tapered = false
  TaperedAngle = 90
  ThreadAngle = 0
  ThreadClass = 0
  ThreadCutOffInner = 0
  ThreadCutOffOuter = 0
  ThreadDirection = 0
  ThreadFit = 0
  ThreadPitch = 0
  ThreadSize = 0
  ThreadType = 0
  Threaded = false
FEATURE [PartDesign::Body] Body004  label="back-plate"
  Group = -> [Sketch009,Pad004,Sketch010,Hole002]
  Origin = -> Origin004
  Placement = pos=(-94,0,0) rot=(0,0,1;0rad)
  Tip = -> Hole002
FEATURE [TechDraw::DrawSVGTemplate] Template001
  EditableTexts = AUTHOR_NAME=LA1RMA; DATE=YYYY-MM-DD; PM=Aircraft aluminium; REVISION=REV A; RIGHTS=License : Creative Commons Zero v1.0 Universal; SCALE=M 1:1; SHEET=1 of 2; SIZE=A1; TITLELINE-1=Mounting box for elevation and azimuth worm drives; TITLELINE-2=RV30 worm gears with Nema23 steppers.; TITLELINE-3=Aircraft aluminium 4mm thick sheets.; TOLERANCE=+/- 0.5
  Height = 594
  Orientation = 1
  Width = 841
FEATURE [TechDraw::DrawViewPart] View001
  CoarseView = false
  Direction = (0,1,0)
  Focus = 100
  HardHidden = false
  IsoCount = 0
  IsoHidden = false
  IsoVisible = false
  LockPosition = false
  Perspective = false
  Rotation = 0
  ScaleType = 0
  SeamHidden = false
  SeamVisible = true
  SmoothHidden = false
  SmoothVisible = true
  Source = -> [Body008]
  X = 700.862
  XDirection = (-1,0,0)
  Y = 188.508
FEATURE [TechDraw::DrawViewPart] View002
  CoarseView = false
  Direction = (0,1,0)
  Focus = 100
  HardHidden = false
  IsoCount = 0
  IsoHidden = false
  IsoVisible = false
  LockPosition = false
  Perspective = false
  Rotation = 0
  ScaleType = 0
  SeamHidden = false
  SeamVisible = true
  SmoothHidden = false
  SmoothVisible = true
  Source = -> [Body009]
  X = 704.487
  XDirection = (-1,0,0)
  Y = 445.893
FEATURE [TechDraw::DrawViewPart] View003
  CoarseView = false
  Direction = (0,0,-1)
  Focus = 100
  HardHidden = false
  IsoCount = 0
  IsoHidden = false
  IsoVisible = false
  LockPosition = false
  Perspective = false
  Rotation = 0
  ScaleType = 0
  SeamHidden = false
  SeamVisible = true
  SmoothHidden = false
  SmoothVisible = true
  Source = -> [Body006]
  X = 381.849
  XDirection = (1,0,0)
  Y = 459.186
FEATURE [TechDraw::DrawViewPart] View004
  CoarseView = false
  Direction = (0,0,-1)
  Focus = 100
  HardHidden = false
  IsoCount = 0
  IsoHidden = false
  IsoVisible = false
  LockPosition = false
  Perspective = false
  Rotation = 0
  ScaleType = 0
  SeamHidden = false
  SeamVisible = true
  SmoothHidden = false
  SmoothVisible = true
  Source = -> [Body005]
  X = 155.182
  XDirection = (1,0,0)
  Y = 464.36
FEATURE [Sketcher::SketchObject] Sketch021
  MapMode = 5
  Support = -> [XY_Plane010]
  sketch-geometry (1):
    g0: Circle CenterX=-46.1126 CenterY=35.0755 CenterZ=0 NormalX=0 NormalY=0 NormalZ=1 AngleXU=0 Radius=38.7738
FEATURE [PartDesign::Pad] Pad011
  AllowMultiFace = false
  Direction = (1,1,1)
  Length = 10
  Length2 = 100
  Profile = -> Sketch021
  Type = 0
FEATURE [Sketcher::SketchObject] Sketch022
  MapMode = 5
  Placement = pos=(0,0,0) rot=(0.57735,0.57735,0.57735;2.0944rad)
  Support = -> [YZ_Plane010]
  sketch-geometry (1):
    g0: Circle CenterX=35.9745 CenterY=-6.96869 CenterZ=0 NormalX=0 NormalY=0 NormalZ=1 AngleXU=0 Radius=2.5
  constraints (1):
    c: Diameter(g0) = 5
FEATURE [Sketcher::SketchObject] Sketch024
  MapMode = 5
  Placement = pos=(0,0,0) rot=(1,0,0;3.14159rad)
  Support = -> [Pad011]
  sketch-geometry (4):
    g0: LineSegment [constr] StartX=-47 StartY=5 StartZ=0 EndX=-47 EndY=-81 EndZ=0
    g1: LineSegment [constr] StartX=-86 StartY=-36 StartZ=0 EndX=-6 EndY=-36 EndZ=0
    g2: Circle [constr] CenterX=-47 CenterY=-36 CenterZ=0 NormalX=0 NormalY=0 NormalZ=1 AngleXU=0 Radius=7
    g3: Circle CenterX=-47 CenterY=-36 CenterZ=0 NormalX=0 NormalY=0 NormalZ=1 AngleXU=0 Radius=17
  constraints (5):
    c: Vertical(g0)
    c: Horizontal(g1)
    c: PointOnObject(g2,g0)
    c: Diameter(g2) = 14
    c: Coincident(g3,g2)
FEATURE [PartDesign::Pad] Pad012
  AllowMultiFace = false
  BaseFeature = -> Pad011
  Direction = (1,1,1)
  Length = 15
  Length2 = 100
  Profile = -> Sketch024
  Type = 0
FEATURE [Sketcher::SketchObject] Sketch023
  MapMode = 5
  Placement = pos=(0,0,-15) rot=(1,0,0;3.14159rad)
  Support = -> [Pad012]
  sketch-geometry (3):
    g0: LineSegment [constr] StartX=-47.0041 StartY=-17.9869 StartZ=0 EndX=-47.0041 EndY=-57.2105 EndZ=0
    g1: LineSegment [constr] StartX=-67.0883 StartY=-35.9976 StartZ=0 EndX=-26.7183 EndY=-35.9976 EndZ=0
    g2: Circle CenterX=-47.0247 CenterY=-35.9976 CenterZ=0 NormalX=0 NormalY=0 NormalZ=1 AngleXU=0 Radius=7
  constraints (4):
    c: Vertical(g0)
    c: Horizontal(g1)
    c: PointOnObject(g2,g1)
    c: Diameter(g2) = 14
FEATURE [PartDesign::Hole] Hole007
  AllowMultiFace = false
  BaseFeature = -> Pad012
  Depth = 33
  DepthType = 0
  Diameter = 14
  DrillPoint = 1
  DrillPointAngle = 118
  HoleCutCountersinkAngle = 90
  HoleCutDepth = 0
  HoleCutDiameter = 0
  HoleCutType = 0
  ModelActualThread = false
  Profile = -> Sketch023
  Tapered = false
  TaperedAngle = 90
  ThreadAngle = 0
  ThreadClass = 0
  ThreadCutOffInner = 0
  ThreadCutOffOuter = 0
  ThreadDirection = 0
  ThreadFit = 0
  ThreadPitch = 0
  ThreadSize = 0
  ThreadType = 0
  Threaded = false
FEATURE [PartDesign::Hole] Hole008
  AllowMultiFace = false
  BaseFeature = -> Hole007
  Depth = 43
  DepthType = 0
  Diameter = 5.5
  DrillPoint = 1
  DrillPointAngle = 118
  HoleCutCountersinkAngle = 90
  HoleCutDepth = 0
  HoleCutDiameter = 5
  HoleCutType = 0
  ModelActualThread = false
  Profile = -> Sketch022
  Tapered = false
  TaperedAngle = 90
  ThreadAngle = 60
  ThreadClass = 0
  ThreadCutOffInner = 0.0866025
  ThreadCutOffOuter = 0.173205
  ThreadDirection = 0
  ThreadFit = 0
  ThreadPitch = 0.8
  ThreadSize = 0
  ThreadType = 0
  Threaded = false
FEATURE [PartDesign::Body] Body010  label="adapter001"
  Group = -> [Sketch021,Pad011,Sketch024,Pad012,Sketch023,Hole007,Sketch022,Hole008]
  Origin = -> Origin010
  Placement = pos=(1,-55,-178) rot=(1,0,0;1.5708rad)
  Tip = -> Hole008
FEATURE [TechDraw::DrawViewPart] View005
  CoarseView = false
  Direction = (1,0,0)
  Focus = 100
  HardHidden = false
  IsoCount = 0
  IsoHidden = false
  IsoVisible = false
  LockPosition = false
  Perspective = false
  Rotation = 0
  ScaleType = 0
  SeamHidden = false
  SeamVisible = true
  SmoothHidden = false
  SmoothVisible = true
  Source = -> [Body007]
  X = 95.7368
  XDirection = (0,1,0)
  Y = 312.819
FEATURE [TechDraw::DrawViewSection] SectionView  label="Section A - A"
  BaseView = -> View005
  CoarseView = false
  CutSurfaceDisplay = 2
  Direction = (0,0,1)
  FileGeomPattern = <path>
  FileHatchPattern = <path>
  Focus = 100
  FuseBeforeCut = false
  HardHidden = false
  HatchScale = 1
  IsoCount = 0
  IsoHidden = false
  IsoVisible = false
  LockPosition = false
  NameGeomPattern = Diamond
  Perspective = false
  Rotation = 0
  ScaleType = 0
  SeamHidden = false
  SeamVisible = true
  SectionDirection = 3
  SectionNormal = (0,0,1)
  SectionOrigin = (-45.11,35.92,-284.5)
  SectionSymbol = A
  SmoothHidden = false
  SmoothVisible = true
  Source = -> [Body007]
  X = 96.1691
  XDirection = (0,1,0)
  Y = 168.474
FEATURE [TechDraw::DrawViewSection] SectionView001  label="Section B - B"
  BaseView = -> View005
  CoarseView = false
  CutSurfaceDisplay = 2
  Direction = (0,-1,0)
  FileGeomPattern = <path>
  FileHatchPattern = <path>
  Focus = 100
  FuseBeforeCut = false
  HardHidden = false
  HatchScale = 1
  IsoCount = 0
  IsoHidden = false
  IsoVisible = false
  LockPosition = false
  NameGeomPattern = Diamond
  Perspective = false
  Rotation = 0
  ScaleType = 0
  SeamHidden = false
  SeamVisible = true
  SectionDirection = 0
  SectionNormal = (0,-1,0)
  SectionOrigin = (-45.11,35.92,-282.5)
  SectionSymbol = B
  SmoothHidden = false
  SmoothVisible = true
  Source = -> [Body007]
  X = 94.637
  XDirection = (1,0,0)
  Y = 252.023
FEATURE [TechDraw::DrawViewPart] View
  CoarseView = false
  Direction = (-1,0,0)
  Focus = 100
  HardHidden = false
  IsoCount = 0
  IsoHidden = false
  IsoVisible = false
  LockPosition = false
  Perspective = false
  Rotation = 0
  ScaleType = 0
  SeamHidden = false
  SeamVisible = true
  SmoothHidden = false
  SmoothVisible = true
  Source = -> [Body004]
  X = 404.808
  XDirection = (0,-1,0)
  Y = 229.593
FEATURE [TechDraw::DrawViewDimension] Dimension002
  Arbitrary = false
  FormatSpec = ⌀%.2f
  Inverted = false
  LockPosition = false
  MeasureType = 1
  OverTolerance = 0
  References2D = -> [View]
  Rotation = 0
  ScaleType = 0
  TheoreticalExact = false
  Type = 5
  UnderTolerance = 0
  X = -24.7994
  Y = 51.5229
FEATURE [TechDraw::DrawViewDimension] Dimension005
  Arbitrary = false
  FormatSpec = ⌀%.2f
  Inverted = false
  LockPosition = false
  MeasureType = 1
  OverTolerance = 0
  References2D = -> [View]
  Rotation = 0
  ScaleType = 0
  TheoreticalExact = false
  Type = 5
  UnderTolerance = 0
  X = 33.9923
  Y = 4.70333
FEATURE [TechDraw::DrawViewDimension] Dimension004
  Arbitrary = false
  FormatSpec = ⌀%.2f
  Inverted = false
  LockPosition = false
  MeasureType = 1
  OverTolerance = 0
  References2D = -> [View]
  Rotation = 0
  ScaleType = 0
  TheoreticalExact = false
  Type = 5
  UnderTolerance = 0
  X = -41.6886
  Y = 1.7103
FEATURE [TechDraw::DrawViewDimension] Dimension007
  Arbitrary = false
  FormatSpec = ⌀%.2f
  Inverted = false
  LockPosition = false
  MeasureType = 1
  OverTolerance = 0
  References2D = -> [View]
  Rotation = 0
  ScaleType = 0
  TheoreticalExact = false
  Type = 5
  UnderTolerance = 0
  X = 25.0132
  Y = -25.4407
FEATURE [TechDraw::DrawViewDimension] Dimension006
  Arbitrary = false
  FormatSpec = ⌀%.2f
  Inverted = false
  LockPosition = false
  MeasureType = 1
  OverTolerance = 0
  References2D = -> [View]
  Rotation = 0
  ScaleType = 0
  TheoreticalExact = false
  Type = 5
  UnderTolerance = 0
  X = -43.3989
  Y = -23.7304
FEATURE [TechDraw::DrawViewDimension] Dimension
  Arbitrary = false
  FormatSpec = %.2f
  Inverted = false
  LockPosition = false
  MeasureType = 1
  OverTolerance = 0
  References2D = -> [View]
  Rotation = 0
  ScaleType = 0
  TheoreticalExact = false
  Type = 1
  UnderTolerance = 0
  X = -10.4756
  Y = 117.797
FEATURE [TechDraw::DrawViewDimension] Dimension008
  Arbitrary = false
  FormatSpec = ⌀%.2f
  Inverted = false
  LockPosition = false
  MeasureType = 1
  OverTolerance = 0
  References2D = -> [View]
  Rotation = 0
  ScaleType = 0
  TheoreticalExact = false
  Type = 5
  UnderTolerance = 0
  X = -27.7924
  Y = -75.4671
FEATURE [TechDraw::DrawViewDimension] Dimension009
  Arbitrary = false
  FormatSpec = ⌀%.2f
  Inverted = false
  LockPosition = false
  MeasureType = 1
  OverTolerance = 0
  References2D = -> [View]
  Rotation = 0
  ScaleType = 0
  TheoreticalExact = false
  Type = 5
  UnderTolerance = 0
  X = 20.7468
  Y = -80.8662
FEATURE [TechDraw::DrawViewDimension] Dimension003
  Arbitrary = false
  FormatSpec = ⌀%.2f
  Inverted = false
  LockPosition = false
  MeasureType = 1
  OverTolerance = 0
  References2D = -> [View]
  Rotation = 0
  ScaleType = 0
  TheoreticalExact = false
  Type = 5
  UnderTolerance = 0
  X = 28.0062
  Y = 52.1642
FEATURE [TechDraw::DrawViewDimension] Dimension001
  Arbitrary = false
  FormatSpec = %.2f
  Inverted = false
  LockPosition = false
  MeasureType = 1
  OverTolerance = 0
  References2D = -> [View]
  Rotation = 0
  ScaleType = 0
  TheoreticalExact = false
  Type = 2
  UnderTolerance = 0
  X = 77.6033
  Y = -12.5762
FEATURE [TechDraw::DrawViewDimension] Dimension010
  Arbitrary = false
  FormatSpec = %.2f
  Inverted = false
  LockPosition = false
  MeasureType = 1
  OverTolerance = 0
  References2D = -> [View]
  Rotation = 0
  ScaleType = 0
  TheoreticalExact = false
  Type = 1
  UnderTolerance = 0
  X = -77.7472
  Y = -112.023
FEATURE [TechDraw::DrawViewDimension] Dimension011
  Arbitrary = false
  FormatSpec = %.2f
  Inverted = false
  LockPosition = false
  MeasureType = 1
  OverTolerance = 0
  References2D = -> [View]
  Rotation = 0
  ScaleType = 0
  TheoreticalExact = false
  Type = 2
  UnderTolerance = 0
  X = -76.656
  Y = -92.6502
FEATURE [TechDraw::DrawViewDimension] Dimension012
  Arbitrary = false
  FormatSpec = %.2f
  Inverted = false
  LockPosition = false
  MeasureType = 1
  OverTolerance = 0
  References2D = -> [View]
  Rotation = 0
  ScaleType = 0
  TheoreticalExact = false
  Type = 1
  UnderTolerance = 0
  X = 2.30326
  Y = -90.6098
FEATURE [TechDraw::DrawViewDimension] Dimension013
  Arbitrary = false
  FormatSpec = %.2f
  Inverted = false
  LockPosition = false
  MeasureType = 1
  OverTolerance = 0
  References2D = -> [View]
  Rotation = 0
  ScaleType = 0
  TheoreticalExact = false
  Type = 1
  UnderTolerance = 0
  X = -79.9157
  Y = -38.2151
FEATURE [TechDraw::DrawViewDimension] Dimension014
  Arbitrary = false
  FormatSpec = %.2f
  Inverted = false
  LockPosition = false
  MeasureType = 1
  OverTolerance = 0
  References2D = -> [View]
  Rotation = 0
  ScaleType = 0
  TheoreticalExact = false
  Type = 2
  UnderTolerance = 0
  X = -88.718
  Y = -70.7823
FEATURE [TechDraw::DrawViewDimension] Dimension015
  Arbitrary = false
  FormatSpec = %.2f
  Inverted = false
  LockPosition = false
  MeasureType = 1
  OverTolerance = 0
  References2D = -> [View]
  Rotation = 0
  ScaleType = 0
  TheoreticalExact = false
  Type = 1
  UnderTolerance = 0
  X = 2.27074
  Y = -38.2314
FEATURE [TechDraw::DrawViewDimension] Dimension016
  Arbitrary = false
  FormatSpec = %.2f
  Inverted = false
  LockPosition = false
  MeasureType = 1
  OverTolerance = 0
  References2D = -> [View]
  Rotation = 0
  ScaleType = 0
  TheoreticalExact = false
  Type = 2
  UnderTolerance = 0
  X = 32.0224
  Y = -62.8674
FEATURE [TechDraw::DrawViewDimension] Dimension017
  Arbitrary = false
  FormatSpec = %.2f
  Inverted = false
  LockPosition = false
  MeasureType = 1
  OverTolerance = 0
  References2D = -> [View]
  Rotation = 0
  ScaleType = 0
  TheoreticalExact = false
  Type = 1
  UnderTolerance = 0
  X = -79.7188
  Y = -4.49691
FEATURE [TechDraw::DrawViewDimension] Dimension018
  Arbitrary = false
  FormatSpec = %.2f
  Inverted = false
  LockPosition = false
  MeasureType = 1
  OverTolerance = 0
  References2D = -> [View]
  Rotation = 0
  ScaleType = 0
  TheoreticalExact = false
  Type = 2
  UnderTolerance = 0
  X = -106.283
  Y = -33.9978
FEATURE [TechDraw::DrawViewDimension] Dimension019
  Arbitrary = false
  FormatSpec = %.2f
  Inverted = false
  LockPosition = false
  MeasureType = 1
  OverTolerance = 0
  References2D = -> [View]
  Rotation = 0
  ScaleType = 0
  TheoreticalExact = false
  Type = 1
  UnderTolerance = 0
  X = 20.1301
  Y = -4.58849
FEATURE [TechDraw::DrawViewDimension] Dimension020
  Arbitrary = false
  FormatSpec = %.2f
  Inverted = false
  LockPosition = false
  MeasureType = 1
  OverTolerance = 0
  References2D = -> [View]
  Rotation = 0
  ScaleType = 0
  TheoreticalExact = false
  Type = 2
  UnderTolerance = 0
  X = 49.4485
  Y = -27.5575
FEATURE [TechDraw::DrawViewDimension] Dimension021
  Arbitrary = false
  FormatSpec = %.2f
  Inverted = false
  LockPosition = false
  MeasureType = 1
  OverTolerance = 0
  References2D = -> [View]
  Rotation = 0
  ScaleType = 0
  TheoreticalExact = false
  Type = 2
  UnderTolerance = 0
  X = -106.24
  Y = 28.8653
FEATURE [TechDraw::DrawViewDimension] Dimension022
  Arbitrary = false
  FormatSpec = %.2f
  Inverted = false
  LockPosition = false
  MeasureType = 1
  OverTolerance = 0
  References2D = -> [View]
  Rotation = 0
  ScaleType = 0
  TheoreticalExact = false
  Type = 1
  UnderTolerance = 0
  X = -32.9636
  Y = 67.5421
FEATURE [TechDraw::DrawViewDimension] Dimension023
  Arbitrary = false
  FormatSpec = %.2f
  Inverted = false
  LockPosition = false
  MeasureType = 1
  OverTolerance = 0
  References2D = -> [View]
  Rotation = 0
  ScaleType = 0
  TheoreticalExact = false
  Type = 2
  UnderTolerance = 0
  X = 65.123
  Y = 31.8202
FEATURE [TechDraw::DrawViewDimension] Dimension024
  Arbitrary = false
  FormatSpec = %.2f
  Inverted = false
  LockPosition = false
  MeasureType = 1
  OverTolerance = 0
  References2D = -> [View]
  Rotation = 0
  ScaleType = 0
  TheoreticalExact = false
  Type = 1
  UnderTolerance = 0
  X = 19.963
  Y = 67.5465
FEATURE [TechDraw::DrawViewDimension] Dimension025
  Arbitrary = false
  FormatSpec = R%.2f
  Inverted = false
  LockPosition = false
  MeasureType = 1
  OverTolerance = 0
  References2D = -> [View001]
  Rotation = 0
  ScaleType = 0
  TheoreticalExact = false
  Type = 4
  UnderTolerance = 0
  X = -101.452
  Y = -21.0982
FEATURE [TechDraw::DrawViewDimension] Dimension026
  Arbitrary = false
  FormatSpec = %.2f
  Inverted = false
  LockPosition = false
  MeasureType = 1
  OverTolerance = 0
  References2D = -> [View001]
  Rotation = 0
  ScaleType = 0
  TheoreticalExact = false
  Type = 2
  UnderTolerance = 0
  X = -178.445
  Y = -54.8896
FEATURE [TechDraw::DrawViewDimension] Dimension027
  Arbitrary = false
  FormatSpec = %.2f
  Inverted = false
  LockPosition = false
  MeasureType = 1
  OverTolerance = 0
  References2D = -> [View001]
  Rotation = 0
  ScaleType = 0
  TheoreticalExact = false
  Type = 2
  UnderTolerance = 0
  X = -83.7047
  Y = -123.326
FEATURE [TechDraw::DrawViewDimension] Dimension028
  Arbitrary = false
  FormatSpec = %.2f
  Inverted = false
  LockPosition = false
  MeasureType = 1
  OverTolerance = 0
  References2D = -> [View001]
  Rotation = 0
  ScaleType = 0
  TheoreticalExact = false
  Type = 2
  UnderTolerance = 0
  X = -71.6406
  Y = 105.032
FEATURE [TechDraw::DrawViewDimension] Dimension029
  Arbitrary = false
  FormatSpec = %.2f
  Inverted = false
  LockPosition = false
  MeasureType = 1
  OverTolerance = 0
  References2D = -> [View001]
  Rotation = 0
  ScaleType = 0
  TheoreticalExact = false
  Type = 1
  UnderTolerance = 0
  X = 0.702578
  Y = 115.931
FEATURE [TechDraw::DrawViewDimension] Dimension030
  Arbitrary = false
  FormatSpec = %.2f
  Inverted = false
  LockPosition = false
  MeasureType = 1
  OverTolerance = 0
  References2D = -> [View001]
  Rotation = 0
  ScaleType = 0
  TheoreticalExact = false
  Type = 1
  UnderTolerance = 0
  X = 28.6467
  Y = 22.5367
FEATURE [TechDraw::DrawViewDimension] Dimension031
  Arbitrary = false
  FormatSpec = %.2f
  Inverted = false
  LockPosition = false
  MeasureType = 1
  OverTolerance = 0
  References2D = -> [View001]
  Rotation = 0
  ScaleType = 0
  TheoreticalExact = false
  Type = 2
  UnderTolerance = 0
  X = -1.93502
  Y = 61.7397
FEATURE [TechDraw::DrawViewDimension] Dimension032
  Arbitrary = false
  FormatSpec = ⌀%.2f
  Inverted = false
  LockPosition = false
  MeasureType = 1
  OverTolerance = 0
  References2D = -> [View001]
  Rotation = 0
  ScaleType = 0
  TheoreticalExact = false
  Type = 5
  UnderTolerance = 0
  X = 31.616
  Y = 40.9837
FEATURE [TechDraw::DrawViewDimension] Dimension033
  Arbitrary = false
  FormatSpec = %.2f
  Inverted = false
  LockPosition = false
  MeasureType = 1
  OverTolerance = 0
  References2D = -> [View001]
  Rotation = 0
  ScaleType = 0
  TheoreticalExact = false
  Type = 2
  UnderTolerance = 0
  X = 66.02
  Y = -18.0328
FEATURE [TechDraw::DrawViewDimension] Dimension034
  Arbitrary = false
  FormatSpec = %.2f
  Inverted = false
  LockPosition = false
  MeasureType = 1
  OverTolerance = 0
  References2D = -> [View001]
  Rotation = 0
  ScaleType = 0
  TheoreticalExact = false
  Type = 1
  UnderTolerance = 0
  X = -52.0805
  Y = -7.291
FEATURE [TechDraw::DrawViewDimension] Dimension035
  Arbitrary = false
  FormatSpec = R%.2f
  Inverted = false
  LockPosition = false
  MeasureType = 1
  OverTolerance = 0
  References2D = -> [View002]
  Rotation = 0
  ScaleType = 0
  TheoreticalExact = false
  Type = 4
  UnderTolerance = 0
  X = -98.1268
  Y = -11.7096
FEATURE [TechDraw::DrawViewDimension] Dimension036
  Arbitrary = false
  FormatSpec = %.2f
  Inverted = false
  LockPosition = false
  MeasureType = 1
  OverTolerance = 0
  References2D = -> [View002]
  Rotation = 0
  ScaleType = 0
  TheoreticalExact = false
  Type = 2
  UnderTolerance = 0
  X = 59.9984
  Y = 0.80937
FEATURE [TechDraw::DrawViewDimension] Dimension037
  Arbitrary = false
  FormatSpec = %.2f
  Inverted = false
  LockPosition = false
  MeasureType = 1
  OverTolerance = 0
  References2D = -> [View002]
  Rotation = 0
  ScaleType = 0
  TheoreticalExact = false
  Type = 1
  UnderTolerance = 0
  X = -0.80937
  Y = 120.045
FEATURE [TechDraw::DrawViewDimension] Dimension038
  Arbitrary = false
  FormatSpec = %.2f
  Inverted = false
  LockPosition = false
  MeasureType = 1
  OverTolerance = 0
  References2D = -> [View002]
  Rotation = 0
  ScaleType = 0
  TheoreticalExact = false
  Type = 2
  UnderTolerance = 0
  X = -175.443
  Y = -53.1472
FEATURE [TechDraw::DrawViewDimension] Dimension039
  Arbitrary = false
  FormatSpec = %.2f
  Inverted = false
  LockPosition = false
  MeasureType = 1
  OverTolerance = 0
  References2D = -> [View002]
  Rotation = 0
  ScaleType = 0
  TheoreticalExact = false
  Type = 1
  UnderTolerance = 0
  X = -55.2318
  Y = 2.41957
FEATURE [TechDraw::DrawViewDimension] Dimension040
  Arbitrary = false
  FormatSpec = %.2f
  Inverted = false
  LockPosition = false
  MeasureType = 1
  OverTolerance = 0
  References2D = -> [View002]
  Rotation = 0
  ScaleType = 0
  TheoreticalExact = false
  Type = 2
  UnderTolerance = 0
  X = -69.5425
  Y = 104.881
FEATURE [TechDraw::DrawViewDimension] Dimension041
  Arbitrary = false
  FormatSpec = %.2f
  Inverted = false
  LockPosition = false
  MeasureType = 1
  OverTolerance = 0
  References2D = -> [View002]
  Rotation = 0
  ScaleType = 0
  TheoreticalExact = false
  Type = 2
  UnderTolerance = 0
  X = -71.7011
  Y = -89.821
FEATURE [TechDraw::DrawViewDimension] Dimension042
  Arbitrary = false
  FormatSpec = %.2f
  Inverted = false
  LockPosition = false
  MeasureType = 1
  OverTolerance = 0
  References2D = -> [View004]
  Rotation = 0
  ScaleType = 0
  TheoreticalExact = false
  Type = 2
  UnderTolerance = 0
  X = 96.6979
  Y = -2.12789
FEATURE [TechDraw::DrawViewDimension] Dimension043
  Arbitrary = false
  FormatSpec = %.2f
  Inverted = false
  LockPosition = false
  MeasureType = 1
  OverTolerance = 0
  References2D = -> [View004]
  Rotation = 0
  ScaleType = 0
  TheoreticalExact = false
  Type = 1
  UnderTolerance = 0
  X = 2.12789
  Y = -83.9388
FEATURE [TechDraw::DrawViewDimension] Dimension044
  Arbitrary = false
  FormatSpec = %.2f
  Inverted = false
  LockPosition = false
  MeasureType = 1
  OverTolerance = 0
  References2D = -> [View003]
  Rotation = 0
  ScaleType = 0
  TheoreticalExact = false
  Type = 1
  UnderTolerance = 0
  X = -63.1151
  Y = -1.78889
FEATURE [TechDraw::DrawViewDimension] Dimension045
  Arbitrary = false
  FormatSpec = %.2f
  Inverted = false
  LockPosition = false
  MeasureType = 1
  OverTolerance = 0
  References2D = -> [View003]
  Rotation = 0
  ScaleType = 0
  TheoreticalExact = false
  Type = 2
  UnderTolerance = 0
  X = -43.1013
  Y = -33.931
FEATURE [TechDraw::DrawViewDimension] Dimension046
  Arbitrary = false
  FormatSpec = %.2f
  Inverted = false
  LockPosition = false
  MeasureType = 1
  OverTolerance = 0
  References2D = -> [View003]
  Rotation = 0
  ScaleType = 0
  TheoreticalExact = false
  Type = 1
  UnderTolerance = 0
  X = -1.28273
  Y = 73.5996
FEATURE [TechDraw::DrawViewDimension] Dimension047
  Arbitrary = false
  FormatSpec = %.2f
  Inverted = false
  LockPosition = false
  MeasureType = 1
  OverTolerance = 0
  References2D = -> [View003]
  Rotation = 0
  ScaleType = 0
  TheoreticalExact = false
  Type = 2
  UnderTolerance = 0
  X = 96.7836
  Y = 1.53927
FEATURE [TechDraw::DrawViewDimension] Dimension048
  Arbitrary = false
  FormatSpec = ⌀%.2f
  Inverted = false
  LockPosition = false
  MeasureType = 1
  OverTolerance = 0
  References2D = -> [View003]
  Rotation = 0
  ScaleType = 0
  TheoreticalExact = false
  Type = 5
  UnderTolerance = 0
  X = -4.10473
  Y = 23.3456
FEATURE [TechDraw::DrawViewDimension] Dimension049
  Arbitrary = false
  FormatSpec = ⌀%.2f
  Inverted = false
  LockPosition = false
  MeasureType = 1
  OverTolerance = 0
  References2D = -> [SectionView]
  Rotation = 0
  ScaleType = 0
  TheoreticalExact = false
  Type = 5
  UnderTolerance = 0
  X = 20.9928
  Y = 23.2685
FEATURE [TechDraw::DrawViewDimension] Dimension050
  Arbitrary = false
  FormatSpec = ⌀%.2f
  Inverted = false
  LockPosition = false
  MeasureType = 1
  OverTolerance = 0
  References2D = -> [SectionView]
  Rotation = 0
  ScaleType = 0
  TheoreticalExact = false
  Type = 5
  UnderTolerance = 0
  X = 55.3333
  Y = 16.4137
FEATURE [TechDraw::DrawViewDimension] Dimension052
  Arbitrary = false
  FormatSpec = %.2f
  Inverted = false
  LockPosition = false
  MeasureType = 1
  OverTolerance = 0
  References2D = -> [SectionView001]
  Rotation = 0
  ScaleType = 0
  TheoreticalExact = false
  Type = 2
  UnderTolerance = 0
  X = -61.396
  Y = 6.46058
FEATURE [TechDraw::DrawViewDimension] Dimension053
  Arbitrary = false
  FormatSpec = %.2f
  Inverted = false
  LockPosition = false
  MeasureType = 1
  OverTolerance = 0
  References2D = -> [SectionView001]
  Rotation = 0
  ScaleType = 0
  TheoreticalExact = false
  Type = 2
  UnderTolerance = 0
  X = -53.5836
  Y = -27.1104
FEATURE [TechDraw::DrawViewDimension] Dimension054
  Arbitrary = false
  FormatSpec = %.2f
  Inverted = false
  LockPosition = false
  MeasureType = 1
  OverTolerance = 0
  References2D = -> [SectionView001]
  Rotation = 0
  ScaleType = 0
  TheoreticalExact = false
  Type = 2
  UnderTolerance = 0
  X = 52.605
  Y = 21.7862
FEATURE [TechDraw::DrawViewDimension] Dimension055
  Arbitrary = false
  FormatSpec = %.2f
  Inverted = false
  LockPosition = false
  MeasureType = 1
  OverTolerance = 0
  References2D = -> [SectionView001]
  Rotation = 0
  ScaleType = 0
  TheoreticalExact = false
  Type = 2
  UnderTolerance = 0
  X = 40.9345
  Y = 25.5021
FEATURE [TechDraw::DrawViewDimension] Dimension056
  Arbitrary = false
  FormatSpec = %.2f
  Inverted = false
  LockPosition = false
  MeasureType = 1
  OverTolerance = 0
  References2D = -> [SectionView001]
  Rotation = 0
  ScaleType = 0
  TheoreticalExact = false
  Type = 2
  UnderTolerance = 0
  X = 52.6902
  Y = -12.2236
FEATURE [TechDraw::DrawSVGTemplate] Template002
  EditableTexts = AUTHOR_NAME=LA1RMA; DATE=YYYY-MM-DD; PM=aircraft aluminium; REVISION=REV A; RIGHTS=License : Creative Commons Zero v1.0 Universal; SCALE=M 1:1; SHEET=2 of 2; SIZE=A1; TITLELINE-1=Different assembly views.; TITLELINE-2=Will fit in a ABS box measuring minimum:; TITLELINE-3=Depth 171 X With 128 X Height 215mm; TOLERANCE=+/- 0.5mm
  Height = 594
  Orientation = 1
  Width = 841
FEATURE [App::Link] Link  label="motor001"
  LinkTransform = true
  LinkedObject = -> Body001
FEATURE [App::Link] Link001  label="motor-mount001"
  LinkTransform = true
  LinkedObject = -> Body
FEATURE [App::Link] Link002  label="gearbox001"
  LinkTransform = true
  LinkedObject = -> Body002
FEATURE [App::Link] Link003  label="Body004"
  LinkTransform = true
  LinkedObject = -> Body003
FEATURE [App::LinkGroup] LinkGroup
  ElementList = -> [Link,Link001,Link002,Link003]
  LinkMode = 1
  Placement = pos=(0,-107.605,-260.605) rot=(1,0,0;1.5708rad)
FEATURE [App::Link] Link004  label="motor002"
  LinkTransform = true
  LinkedObject = -> Body001
FEATURE [App::Link] Link005  label="motor-mount002"
  LinkTransform = true
  LinkedObject = -> Body
FEATURE [App::Link] Link006  label="gearbox002"
  LinkTransform = true
  LinkedObject = -> Body002
FEATURE [App::Link] Link007  label="Body005"
  LinkTransform = true
  LinkedObject = -> Body003
FEATURE [App::LinkGroup] LinkGroup001
  ElementList = -> [Link004,Link005,Link006,Link007]
  LinkMode = 1
  Placement = pos=(0,-32,0) rot=(0,0,1;0rad)
FEATURE [TechDraw::DrawViewPart] View006
  CoarseView = false
  Direction = (0.707,0.707,0)
  Focus = 100
  HardHidden = false
  IsoCount = 0
  IsoHidden = false
  IsoVisible = false
  LockPosition = false
  Perspective = false
  Rotation = 0
  ScaleType = 0
  SeamHidden = false
  SeamVisible = true
  SmoothHidden = false
  SmoothVisible = true
  Source = -> [Body010,Body004,Body009,Body008,Body007,Body006,Body005]
  X = 148.563
  XDirection = (-0.707,0.707,0)
  Y = 442.174
FEATURE [TechDraw::DrawViewPart] View007
  CoarseView = false
  Direction = (1,0,0)
  Focus = 100
  HardHidden = false
  IsoCount = 0
  IsoHidden = false
  IsoVisible = false
  LockPosition = false
  Perspective = false
  Rotation = 0
  ScaleType = 0
  SeamHidden = false
  SeamVisible = true
  SmoothHidden = false
  SmoothVisible = true
  Source = -> [Body010,Body004,Body009,Body008,Body007,Body006,Body005]
  X = 408.845
  XDirection = (0,1,0)
  Y = 442.638
FEATURE [TechDraw::DrawViewPart] View008
  CoarseView = false
  Direction = (0.707,-0.707,0)
  Focus = 100
  HardHidden = false
  IsoCount = 0
  IsoHidden = false
  IsoVisible = false
  LockPosition = false
  Perspective = false
  Rotation = 0
  ScaleType = 0
  SeamHidden = false
  SeamVisible = true
  SmoothHidden = false
  SmoothVisible = true
  Source = -> [Body005,Body006,Body007,Body008,Body009,Body004,Body010]
  X = 653.963
  XDirection = (0.707,0.707,0)
  Y = 442.715
FEATURE [TechDraw::DrawViewPart] View009
  CoarseView = false
  Direction = (0.707,-0.707,0)
  Focus = 100
  HardHidden = false
  IsoCount = 0
  IsoHidden = false
  IsoVisible = false
  LockPosition = false
  Perspective = false
  Rotation = 0
  ScaleType = 0
  SeamHidden = false
  SeamVisible = true
  SmoothHidden = false
  SmoothVisible = true
  Source = -> [Body004,Body009,Body008,Body006,Body005]
  X = 155.51
  XDirection = (0.707,0.707,0)
  Y = 157.617
FEATURE [TechDraw::DrawViewPart] View010
  CoarseView = false
  Direction = (0.658,-0.636,0.403)
  Focus = 100
  HardHidden = false
  IsoCount = 0
  IsoHidden = false
  IsoVisible = false
  LockPosition = false
  Perspective = false
  Rotation = 0
  ScaleType = 0
  SeamHidden = false
  SeamVisible = true
  SmoothHidden = false
  SmoothVisible = true
  Source = -> [Body005,Body006,Body008,Body009,Body004]
  X = 406.445
  XDirection = (0.69,0.724,0.016)
  Y = 158.583
FEATURE [TechDraw::DrawViewPart] View011
  CoarseView = false
  Direction = (0.928,-0.324,-0.182)
  Focus = 100
  HardHidden = false
  IsoCount = 0
  IsoHidden = false
  IsoVisible = false
  LockPosition = false
  Perspective = false
  Rotation = 0
  ScaleType = 0
  SeamHidden = false
  SeamVisible = true
  SmoothHidden = false
  SmoothVisible = true
  Source = -> [Body010,Body004,Body009,Body008,Body007,Body006,Body005]
  X = 627.557
  XDirection = (0.331,0.944,0.009)
  XSource = -> [LinkGroup001,LinkGroup]
  Y = 163.678
FEATURE [TechDraw::DrawPage] Page002
  KeepUpdated = true
  NextBalloonIndex = 1
  ProjectionType = 0
  Template = -> Template002
  Views = -> [View006,View007,View008,View009,View010,View011]
FEATURE [TechDraw::DrawViewDimension] Dimension057
  Arbitrary = false
  FormatSpec = %.2f
  Inverted = false
  LockPosition = false
  MeasureType = 1
  OverTolerance = 0
  References2D = -> [SectionView001]
  Rotation = 0
  ScaleType = 0
  TheoreticalExact = false
  Type = 1
  UnderTolerance = 0
  X = -2.09406
  Y = -29.3834
FEATURE [TechDraw::DrawViewDimension] Dimension058
  Arbitrary = false
  FormatSpec = ⌀%.2f
  Inverted = false
  LockPosition = false
  MeasureType = 1
  OverTolerance = 0
  References2D = -> [View005]
  Rotation = 0
  ScaleType = 0
  TheoreticalExact = false
  Type = 5
  UnderTolerance = 0
  X = 25.9031
  Y = 17.2688
FEATURE [TechDraw::DrawPage] Page001
  KeepUpdated = true
  NextBalloonIndex = 1
  ProjectionType = 0
  Template = -> Template001
  Views = -> [View,View001,View002,View003,View004,View005,SectionView,SectionView001,Dimension,Dimension001,Dimension002,Dimension003,Dimension004,Dimension005,Dimension006,Dimension007,Dimension008,Dimension009,Dimension010,Dimension011,Dimension012,Dimension013,Dimension014,Dimension015,Dimension016,Dimension017,Dimension018,Dimension019,Dimension020,Dimension021,Dimension022,Dimension023,Dimension024,+33 more]
note: 4 file-system paths scrubbed to <path> (originals preserved in the JSON sidecar)
